# Revit family: FantiniCosmi_BIM_B12CN
name_source: partatom
category: Generic Models
units: mm (PartAtom-declared; Revit-internal decimal feet)

## family parameters
Always vertical = Yes
Can host rebar = No
Cut with Voids When Loaded = No
Part Type = Normal
Room Calculation Point = No
Round Connector Dimension = Use Diameter
Shared = No
Work Plane-Based = No

## types (1)
- Standard
    Catalog web link = https://www.fantinicosmi.it
    Connection G 1/4 = Female
    Default Elevation = 0 mm  [stored 0 ft]
    Description = Pressure switches up to 28 bar with adjustable differential
    Designer = Carniti
    Differential = 0.6 ÷ 3 bar
    Part Number = B12CN
    Pressure switch body admissible temperature = -35 ÷ 60°C
    Protection degree = IP40
    Range = -0.2 ÷ 8 bar
    Reset = Automatic
    Sensitive element max. pressure = 9 bar
    Storage and transport temperature = -35 ÷ 60°C
    Weight = 0.44 Kg

note: [stored X ft] marks values corroborated as IEEE doubles in the binary element streams (Revit-internal decimal feet)

## geometry (parser evidence)
native form markers: Sweep x3
no freeform markers — native parametric forms only
